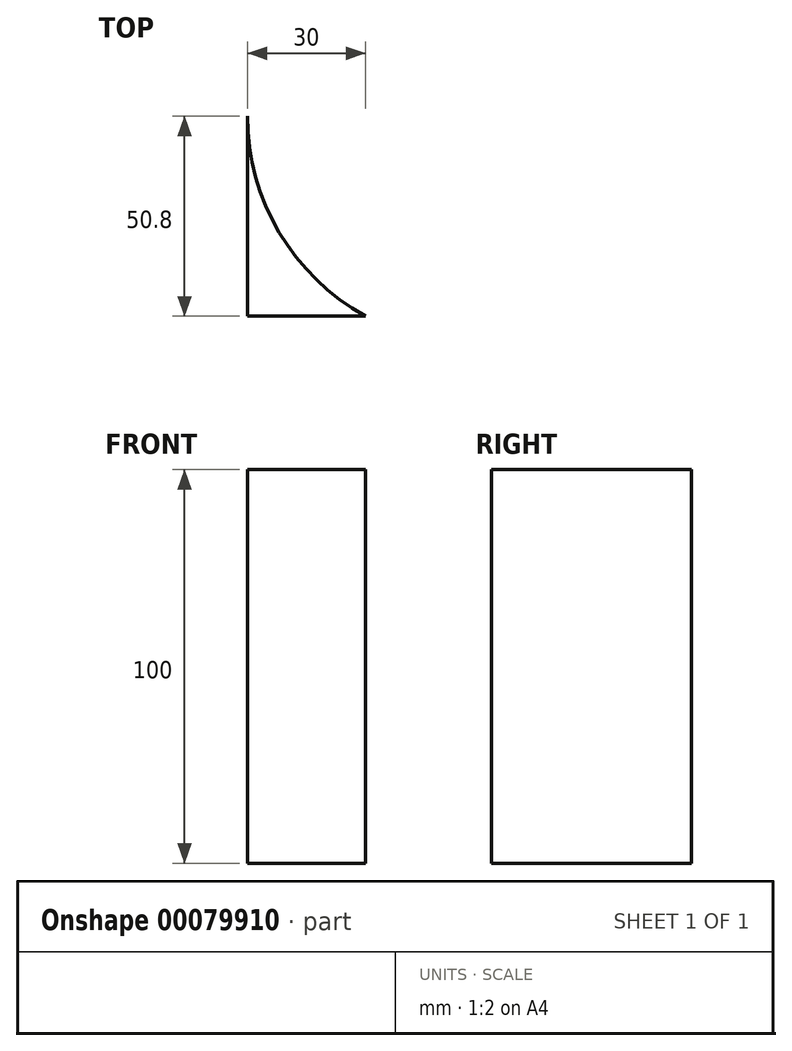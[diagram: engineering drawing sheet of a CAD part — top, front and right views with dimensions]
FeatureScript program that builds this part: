
annotation { "Feature Type Name" : "Feature", "Feature Type Description" : "" }
export const myFeature = defineFeature(function(context is Context, id is Id, definition is map)
    precondition{}
    {
        {
            var Q0;
            Q0=qCreatedBy(makeId("Top.planeOp"),FACE);
            var sketch = newSketch(context, id + "F0", { "sketchPlane" : qUnion([Q0])});
            skLineSegment(sketch, "E0", {"start": v(0, 50.8) * mm, "end": v(0, 0) * mm});
            skLineSegment(sketch, "E1", {"start": v(0, 0) * mm, "end": v(30, 0) * mm});
            skArc(sketch, "E2", {"start": v(0, 50.8) * mm, "mid": v(8.06, 21.3) * mm, "end": v(30, 0) * mm});
            skSolve(sketch);
        }
        {
            var Q0;
            Q0=makeQuery(id+"F0.imprint","IMPRINT",FACE,{"disambiguationData":[TD([[makeQuery(id+"F0.imprint","IMPRINT",EDGE,{"derivedFrom":sQuery(id+"F0.wireOp",EDGE,"E0")}),1.0]])]});
            extrude(context, id + "F1", {"entities" : qUnion([Q0]), "depth" : 50 * mm});
        }
        {
            var Q0;
            Q0=makeQuery(id+"F1.opExtrude","CAP_FACE",FACE,{"disambiguationData":[OSD([sQuery(id+"F0.wireOp",EDGE,"E0"),sQuery(id+"F0.wireOp",EDGE,"E1"),sQuery(id+"F0.wireOp",EDGE,"E2")])],"isStart":true});
            extrude(context, id + "F2", {"entities" : qUnion([Q0]), "operationType" : NewBodyOperationType.ADD, "depth" : 50 * mm});
        }
    });
